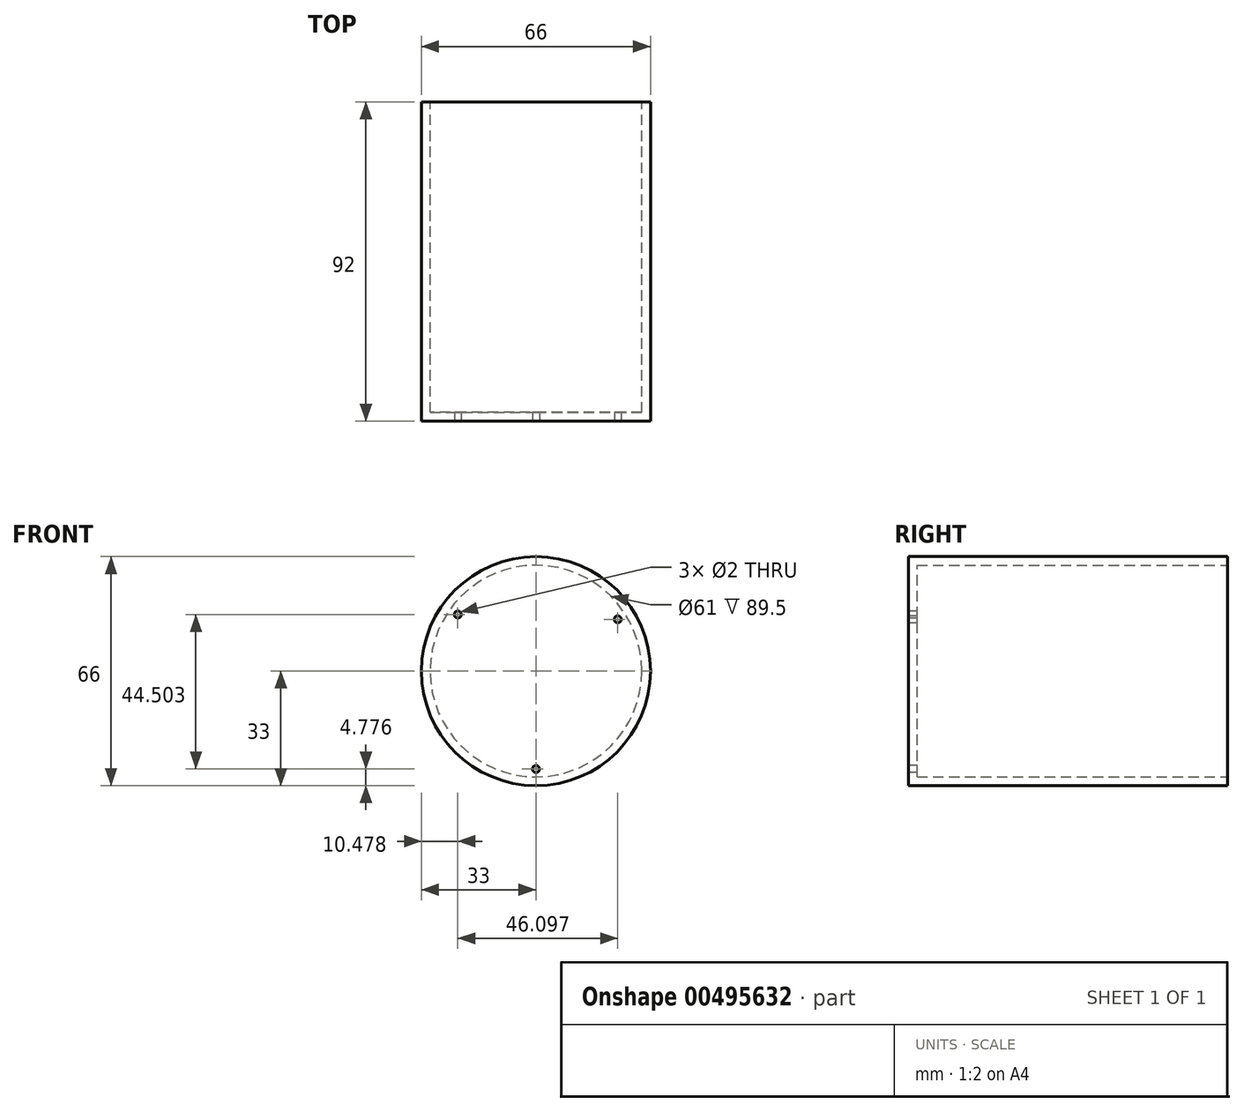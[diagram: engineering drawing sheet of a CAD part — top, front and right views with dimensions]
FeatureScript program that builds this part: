
annotation { "Feature Type Name" : "Feature", "Feature Type Description" : "" }
export const myFeature = defineFeature(function(context is Context, id is Id, definition is map)
    precondition{}
    {
        {
            var Q0;
            Q0=qCreatedBy(makeId("Front.planeOp"),FACE);
            var sketch = newSketch(context, id + "F0", { "sketchPlane" : qUnion([Q0])});
            skCircle(sketch, "E0", {"center": v(0, 0) * mm, "radius": 33 * mm});
            skCircle(sketch, "E1", {"center": v(0, 0) * mm, "radius": 30 * mm});
            skSolve(sketch);
        }
        {
            var Q0;
            Q0=makeQuery(id+"F0.imprint","IMPRINT",FACE,{"disambiguationData":[TD([[makeQuery(id+"F0.imprint","IMPRINT",EDGE,{"derivedFrom":sQuery(id+"F0.wireOp",EDGE,"E0")}),1.0]])]});
            var Q1;
            Q1=makeQuery(id+"F0.imprint","IMPRINT",FACE,{"disambiguationData":[TD([[makeQuery(id+"F0.imprint","IMPRINT",EDGE,{"derivedFrom":sQuery(id+"F0.wireOp",EDGE,"E1")}),1.0]])]});
            extrude(context, id + "F1", {"entities" : qUnion([Q0, Q1]), "depth" : 92 * mm});
        }
        {
            var Q0;
            Q0=qSketchRegion(id+"F0",true);
            extrude(context, id + "F2", {"entities" : qUnion([Q0]), "operationType" : NewBodyOperationType.ADD, "depth" : 3 * mm});
        }
        {
            var Q0;
            Q0=makeQuery(id+"F1.opExtrude","CAP_FACE",FACE,{"disambiguationData":[OSD([sQuery(id+"F0.wireOp",EDGE,"E0"),sQuery(id+"F0.wireOp",EDGE,"8NhZ6zUw-aQF8-c4Ss-Shcg-NumPj7j0fB0R"),sQuery(id+"F0.wireOp",EDGE,"cyOrEb9H-zXSa-neom-TAE1-iIaJjLYwJ2em"),sQuery(id+"F0.wireOp",EDGE,"eCSrJlCN-44u3-emCK-dKCq-qSBNGMtWKpVP")])],"isStart":true});
            shell(context, id + "F3", {"entities" : qUnion([Q0]), "thickness" : 2.5 * mm});
        }
        {
            var Q0;
            Q0=makeQuery(id+"F1.opExtrude","CAP_FACE",FACE,{"disambiguationData":[OSD([sQuery(id+"F0.wireOp",EDGE,"E0")])],"isStart":false});
            var sketch = newSketch(context, id + "F4", { "sketchPlane" : qUnion([Q0])});
            skCircle(sketch, "E2", {"center": v(0, -28.22) * mm, "radius": 1 * mm});
            skCircle(sketch, "E3", {"center": v(23.58, 14.91) * mm, "radius": 1 * mm});
            skCircle(sketch, "E4", {"center": v(-22.52, 16.28) * mm, "radius": 1 * mm});
            skSolve(sketch);
        }
        {
            var Q0;
            Q0=qSketchRegion(id+"F4",true);
            extrude(context, id + "F5", {"entities" : qUnion([Q0]), "operationType" : NewBodyOperationType.REMOVE, "oppositeDirection" : true, "depth" : 6 * mm});
        }
    });
